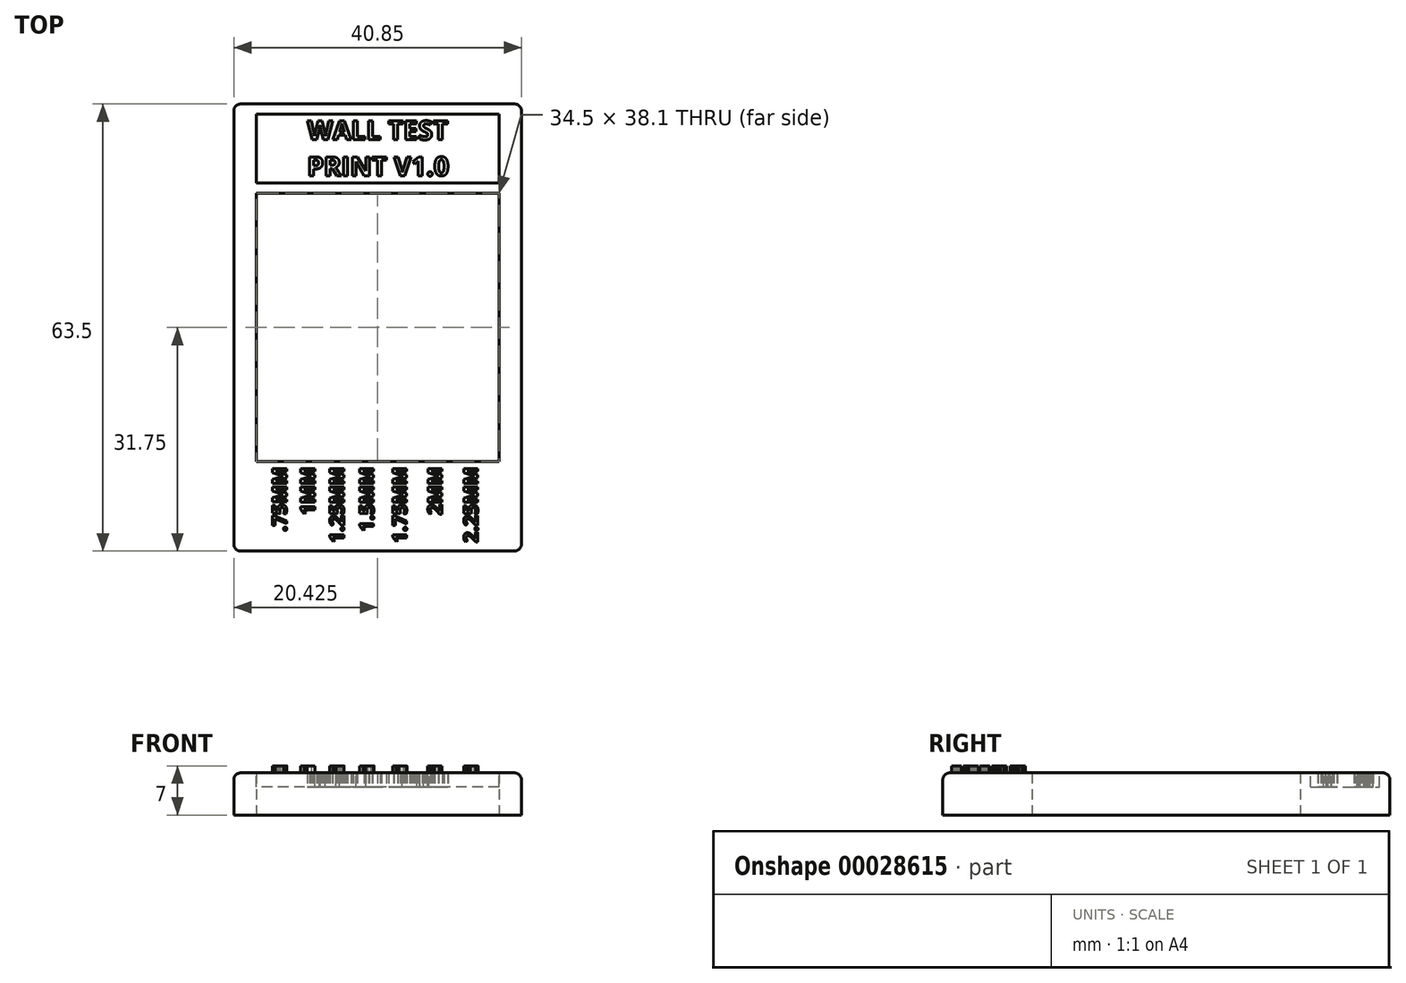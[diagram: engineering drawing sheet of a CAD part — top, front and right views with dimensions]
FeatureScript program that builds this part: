
annotation { "Feature Type Name" : "Feature", "Feature Type Description" : "" }
export const myFeature = defineFeature(function(context is Context, id is Id, definition is map)
    precondition{}
    {
        {
            var Q0;
            Q0=qCreatedBy(makeId("Top.planeOp"),FACE);
            var sketch = newSketch(context, id + "F0", { "sketchPlane" : qUnion([Q0])});
            skLineSegment(sketch, "E0.bottom", {"start": v(0, 0) * mm, "end": v(40.85, 0) * mm});
            skLineSegment(sketch, "E0.top", {"start": v(0, 63.5) * mm, "end": v(40.85, 63.5) * mm});
            skLineSegment(sketch, "E0.left", {"start": v(0, 0) * mm, "end": v(0, 63.5) * mm});
            skLineSegment(sketch, "E0.right", {"start": v(40.85, 0) * mm, "end": v(40.85, 63.5) * mm});
            skLineSegment(sketch, "E1.bottom", {"start": v(3.17, 12.7) * mm, "end": v(37.68, 12.7) * mm});
            skLineSegment(sketch, "E1.top", {"start": v(3.17, 50.8) * mm, "end": v(37.68, 50.8) * mm});
            skLineSegment(sketch, "E1.left", {"start": v(3.17, 12.7) * mm, "end": v(3.17, 50.8) * mm});
            skLineSegment(sketch, "E1.right", {"start": v(37.68, 12.7) * mm, "end": v(37.68, 50.8) * mm});
            skLineSegment(sketch, "E2.bottom", {"start": v(6.17, 50.8) * mm, "end": v(6.92, 50.8) * mm});
            skLineSegment(sketch, "E2.top", {"start": v(6.17, 12.7) * mm, "end": v(6.93, 12.7) * mm});
            skLineSegment(sketch, "E2.left", {"start": v(6.17, 50.8) * mm, "end": v(6.17, 12.7) * mm});
            skLineSegment(sketch, "E2.right", {"start": v(6.92, 50.8) * mm, "end": v(6.92, 12.7) * mm});
            skLineSegment(sketch, "E3.bottom", {"start": v(9.92, 50.8) * mm, "end": v(10.93, 50.8) * mm});
            skLineSegment(sketch, "E3.top", {"start": v(9.93, 12.7) * mm, "end": v(10.93, 12.7) * mm});
            skLineSegment(sketch, "E3.left", {"start": v(9.92, 50.8) * mm, "end": v(9.93, 12.7) * mm});
            skLineSegment(sketch, "E3.right", {"start": v(10.93, 50.8) * mm, "end": v(10.93, 12.7) * mm});
            skLineSegment(sketch, "E4.bottom", {"start": v(13.93, 50.8) * mm, "end": v(15.18, 50.8) * mm});
            skLineSegment(sketch, "E4.top", {"start": v(13.93, 12.7) * mm, "end": v(15.18, 12.7) * mm});
            skLineSegment(sketch, "E4.left", {"start": v(13.93, 50.8) * mm, "end": v(13.93, 12.7) * mm});
            skLineSegment(sketch, "E4.right", {"start": v(15.18, 50.8) * mm, "end": v(15.18, 12.7) * mm});
            skLineSegment(sketch, "E5.top", {"start": v(31.75, 12.7) * mm, "end": v(34.25, 12.7) * mm});
            skLineSegment(sketch, "E6.bottom", {"start": v(18.18, 50.8) * mm, "end": v(19.68, 50.8) * mm});
            skLineSegment(sketch, "E6.top", {"start": v(18.18, 12.7) * mm, "end": v(19.68, 12.7) * mm});
            skLineSegment(sketch, "E6.left", {"start": v(18.18, 50.8) * mm, "end": v(18.18, 12.7) * mm});
            skLineSegment(sketch, "E6.right", {"start": v(19.68, 50.8) * mm, "end": v(19.68, 12.7) * mm});
            skLineSegment(sketch, "E7.bottom", {"start": v(22.68, 50.8) * mm, "end": v(24.43, 50.8) * mm});
            skLineSegment(sketch, "E7.top", {"start": v(22.68, 12.7) * mm, "end": v(24.43, 12.7) * mm});
            skLineSegment(sketch, "E7.left", {"start": v(22.68, 50.8) * mm, "end": v(22.68, 12.7) * mm});
            skLineSegment(sketch, "E7.right", {"start": v(24.43, 50.8) * mm, "end": v(24.43, 12.7) * mm});
            skLineSegment(sketch, "E8.bottom", {"start": v(27.43, 50.8) * mm, "end": v(29.43, 50.8) * mm});
            skLineSegment(sketch, "E8.top", {"start": v(27.43, 12.7) * mm, "end": v(29.43, 12.7) * mm});
            skLineSegment(sketch, "E8.left", {"start": v(27.43, 50.8) * mm, "end": v(27.43, 12.7) * mm});
            skLineSegment(sketch, "E8.right", {"start": v(29.43, 50.8) * mm, "end": v(29.43, 12.7) * mm});
            skLineSegment(sketch, "E9.bottom", {"start": v(32.43, 50.8) * mm, "end": v(34.68, 50.8) * mm});
            skLineSegment(sketch, "E9.top", {"start": v(32.43, 12.7) * mm, "end": v(34.68, 12.7) * mm});
            skLineSegment(sketch, "E9.left", {"start": v(32.43, 50.8) * mm, "end": v(32.43, 12.7) * mm});
            skLineSegment(sketch, "E9.right", {"start": v(34.68, 50.8) * mm, "end": v(34.68, 12.7) * mm});
            skSolve(sketch);
        }
        {
            var Q0;
            Q0 = qSketchRegion(id + "F0", true);
            var Q1;
            Q1=makeQuery(id+"F0.imprint","IMPRINT",FACE,{"disambiguationData":[TD([[makeQuery(id+"F0.imprint","IMPRINT",EDGE,{"derivedFrom":sQuery(id+"F0.wireOp",EDGE,"E2.bottom")}),-1.0]])]});
            var Q2;
            Q2=makeQuery(id+"F0.imprint","IMPRINT",FACE,{"disambiguationData":[TD([[makeQuery(id+"F0.imprint","IMPRINT",EDGE,{"derivedFrom":sQuery(id+"F0.wireOp",EDGE,"E3.bottom")}),-1.0]])]});
            var Q3;
            Q3=makeQuery(id+"F0.imprint","IMPRINT",FACE,{"disambiguationData":[TD([[makeQuery(id+"F0.imprint","IMPRINT",EDGE,{"derivedFrom":sQuery(id+"F0.wireOp",EDGE,"E4.bottom")}),-1.0]])]});
            var Q4;
            Q4=makeQuery(id+"F0.imprint","IMPRINT",FACE,{"disambiguationData":[TD([[makeQuery(id+"F0.imprint","IMPRINT",EDGE,{"derivedFrom":sQuery(id+"F0.wireOp",EDGE,"E5.bottom")}),-1.0]])]});
            var Q5;
            Q5=makeQuery(id+"F0.imprint","IMPRINT",FACE,{"disambiguationData":[TD([[makeQuery(id+"F0.imprint","IMPRINT",EDGE,{"derivedFrom":sQuery(id+"F0.wireOp",EDGE,"E6.bottom")}),-1.0]])]});
            var Q6;
            Q6=makeQuery(id+"F0.imprint","IMPRINT",FACE,{"disambiguationData":[TD([[makeQuery(id+"F0.imprint","IMPRINT",EDGE,{"derivedFrom":sQuery(id+"F0.wireOp",EDGE,"E7.bottom")}),-1.0]])]});
            var Q7;
            Q7=makeQuery(id+"F0.imprint","IMPRINT",FACE,{"disambiguationData":[TD([[makeQuery(id+"F0.imprint","IMPRINT",EDGE,{"derivedFrom":sQuery(id+"F0.wireOp",EDGE,"E8.bottom")}),-1.0]])]});
            var Q8;
            Q8=makeQuery(id+"F0.imprint","IMPRINT",FACE,{"disambiguationData":[TD([[makeQuery(id+"F0.imprint","IMPRINT",EDGE,{"derivedFrom":sQuery(id+"F0.wireOp",EDGE,"E9.bottom")}),-1.0]])]});
            extrude(context, id + "F1", {"entities" : qUnion([Q0, Q1, Q2, Q3, Q4, Q5, Q6, Q7, Q8]), "depth" : 6 * mm});
        }
        {
            var Q0;
            Q0=makeQuery(id+"F1.opExtrude","CAP_FACE",FACE,{"disambiguationData":[OSD([sQuery(id+"F0.wireOp",EDGE,"E0.bottom"),sQuery(id+"F0.wireOp",EDGE,"E0.top"),sQuery(id+"F0.wireOp",EDGE,"E0.left"),sQuery(id+"F0.wireOp",EDGE,"E0.right"),sQuery(id+"F0.wireOp",EDGE,"E1.bottom"),sQuery(id+"F0.wireOp",EDGE,"E1.top"),sQuery(id+"F0.wireOp",EDGE,"E1.left"),sQuery(id+"F0.wireOp",EDGE,"E1.right"),sQuery(id+"F0.wireOp",EDGE,"E2.left"),sQuery(id+"F0.wireOp",EDGE,"E2.right"),sQuery(id+"F0.wireOp",EDGE,"E3.left"),sQuery(id+"F0.wireOp",EDGE,"E3.right"),sQuery(id+"F0.wireOp",EDGE,"E4.left"),sQuery(id+"F0.wireOp",EDGE,"E4.right"),sQuery(id+"F0.wireOp",EDGE,"E5.left"),sQuery(id+"F0.wireOp",EDGE,"E5.right"),sQuery(id+"F0.wireOp",EDGE,"E6.left"),sQuery(id+"F0.wireOp",EDGE,"E6.right")])],"isStart":false});
            var sketch = newSketch(context, id + "F2", { "sketchPlane" : qUnion([Q0])});
            skText(sketch, "E10", { "text": ".75MM", "fontName": "OpenSans-Bold.ttf"});
            const initialGuessF2  = {"E10": [0.00749, 0.00276, 0, 1, 0.002]};
            skSetInitialGuess(sketch, initialGuessF2);
            skSolve(sketch);
        }
        {
            var Q0;
            Q0 = qSketchRegion(id + "F2", true);
            var Q1;
            Q1 = qConstructionFilter(qBodyType(qCreatedBy(id + "F2" ,EDGE), BodyType.WIRE), ConstructionObject.NO);
            extrude(context, id + "F3", {"entities" : qUnion([Q0]), "operationType" : NewBodyOperationType.ADD, "surfaceEntities" : qUnion([Q1]), "depth" : 1 * mm});
        }
        {
            var Q0;
            Q0=makeQuery(id+"F1.opExtrude","CAP_FACE",FACE,{"disambiguationData":[OSD([sQuery(id+"F0.wireOp",EDGE,"E0.bottom"),sQuery(id+"F0.wireOp",EDGE,"E0.top"),sQuery(id+"F0.wireOp",EDGE,"E0.left"),sQuery(id+"F0.wireOp",EDGE,"E0.right"),sQuery(id+"F0.wireOp",EDGE,"E1.bottom"),sQuery(id+"F0.wireOp",EDGE,"E1.top"),sQuery(id+"F0.wireOp",EDGE,"E1.left"),sQuery(id+"F0.wireOp",EDGE,"E1.right"),sQuery(id+"F0.wireOp",EDGE,"E2.left"),sQuery(id+"F0.wireOp",EDGE,"E2.right"),sQuery(id+"F0.wireOp",EDGE,"E3.left"),sQuery(id+"F0.wireOp",EDGE,"E3.right"),sQuery(id+"F0.wireOp",EDGE,"E4.left"),sQuery(id+"F0.wireOp",EDGE,"E4.right"),sQuery(id+"F0.wireOp",EDGE,"E5.top"),sQuery(id+"F0.wireOp",EDGE,"E6.left"),sQuery(id+"F0.wireOp",EDGE,"E6.right"),sQuery(id+"F0.wireOp",EDGE,"E7.left"),sQuery(id+"F0.wireOp",EDGE,"E7.right"),sQuery(id+"F0.wireOp",EDGE,"E8.left"),sQuery(id+"F0.wireOp",EDGE,"E8.right"),sQuery(id+"F0.wireOp",EDGE,"E9.left"),sQuery(id+"F0.wireOp",EDGE,"E9.right")])],"isStart":false});
            var sketch = newSketch(context, id + "F4", { "sketchPlane" : qUnion([Q0])});
            skLineSegment(sketch, "E11", {"start": v(3.17, 50.8) * mm, "end": v(3.17, 63.5) * mm, "construction": true});
            skLineSegment(sketch, "E12", {"start": v(37.68, 50.8) * mm, "end": v(37.68, 63.5) * mm, "construction": true});
            skLineSegment(sketch, "E13", {"start": v(3.17, 57.15) * mm, "end": v(37.68, 57.15) * mm, "construction": true});
            skLineSegment(sketch, "E14", {"start": v(20.42, 57.15) * mm, "end": v(20.42, 63.5) * mm, "construction": true});
            skLineSegment(sketch, "E15.rect.bottom", {"start": v(37.67, 52.25) * mm, "end": v(3.18, 52.25) * mm});
            skLineSegment(sketch, "E15.rect.top", {"start": v(37.68, 62.05) * mm, "end": v(3.18, 62.05) * mm});
            skLineSegment(sketch, "E15.rect.left", {"start": v(37.68, 52.25) * mm, "end": v(37.68, 62.05) * mm});
            skLineSegment(sketch, "E15.rect.right", {"start": v(3.18, 52.25) * mm, "end": v(3.18, 62.05) * mm});
            skPoint(sketch, "E15.rect.middle", {"position": v(20.42, 57.15) * mm});
            skSolve(sketch);
        }
        {
            var Q0;
            Q0 = qSketchRegion(id + "F4", true);
            extrude(context, id + "F5", {"entities" : qUnion([Q0]), "operationType" : NewBodyOperationType.REMOVE, "oppositeDirection" : true, "depth" : 2 * mm});
        }
        {
            var Q0;
            Q0=makeQuery(id+"F5.boolean.opBoolean","COPY",FACE,{"derivedFrom":makeQuery(id+"F5.opExtrude","CAP_FACE",FACE,{"disambiguationData":[OSD([sQuery(id+"F4.wireOp",EDGE,"E15.rect.bottom"),sQuery(id+"F4.wireOp",EDGE,"E15.rect.top"),sQuery(id+"F4.wireOp",EDGE,"E15.rect.left"),sQuery(id+"F4.wireOp",EDGE,"E15.rect.right")])],"isStart":false})});
            var sketch = newSketch(context, id + "F6", { "sketchPlane" : qUnion([Q0])});
            skText(sketch, "E16", { "text": "WALL TEST\nPRINT V1.0", "fontName": "OpenSans-Bold.ttf"});
            skLineSegment(sketch, "E17", {"start": v(20.43, 62.05) * mm, "end": v(20.43, 52.25) * mm, "construction": true});
            const initialGuessF6  = {"E16": [0.01043, 0.05842, 1, 0, 0.00271]};
            skSetInitialGuess(sketch, initialGuessF6);
            skSolve(sketch);
        }
        {
            var Q0;
            Q0 = qSketchRegion(id + "F6", true);
            extrude(context, id + "F7", {"entities" : qUnion([Q0]), "operationType" : NewBodyOperationType.ADD, "depth" : 2 * mm});
        }
        {
            var Q0;
            Q0=makeQuery(id+"F1.opExtrude","CAP_FACE",FACE,{"disambiguationData":[OSD([sQuery(id+"F0.wireOp",EDGE,"E0.bottom"),sQuery(id+"F0.wireOp",EDGE,"E0.top"),sQuery(id+"F0.wireOp",EDGE,"E0.left"),sQuery(id+"F0.wireOp",EDGE,"E0.right"),sQuery(id+"F0.wireOp",EDGE,"E1.bottom"),sQuery(id+"F0.wireOp",EDGE,"E1.top"),sQuery(id+"F0.wireOp",EDGE,"E1.left"),sQuery(id+"F0.wireOp",EDGE,"E1.right"),sQuery(id+"F0.wireOp",EDGE,"E2.left"),sQuery(id+"F0.wireOp",EDGE,"E2.right"),sQuery(id+"F0.wireOp",EDGE,"E3.left"),sQuery(id+"F0.wireOp",EDGE,"E3.right"),sQuery(id+"F0.wireOp",EDGE,"E4.left"),sQuery(id+"F0.wireOp",EDGE,"E4.right"),sQuery(id+"F0.wireOp",EDGE,"E5.top"),sQuery(id+"F0.wireOp",EDGE,"E6.left"),sQuery(id+"F0.wireOp",EDGE,"E6.right"),sQuery(id+"F0.wireOp",EDGE,"E7.left"),sQuery(id+"F0.wireOp",EDGE,"E7.right"),sQuery(id+"F0.wireOp",EDGE,"E8.left"),sQuery(id+"F0.wireOp",EDGE,"E8.right"),sQuery(id+"F0.wireOp",EDGE,"E9.left"),sQuery(id+"F0.wireOp",EDGE,"E9.right")])],"isStart":false});
            var sketch = newSketch(context, id + "F8", { "sketchPlane" : qUnion([Q0])});
            skText(sketch, "E18", { "text": "1MM", "fontName": "OpenSans-Bold.ttf"});
            skText(sketch, "E19", { "text": "1.25MM", "fontName": "OpenSans-Bold.ttf"});
            skText(sketch, "E20", { "text": "1.5MM", "fontName": "OpenSans-Bold.ttf"});
            skText(sketch, "E21", { "text": "1.75MM", "fontName": "OpenSans-Bold.ttf"});
            skText(sketch, "E22", { "text": "2MM", "fontName": "OpenSans-Bold.ttf"});
            skText(sketch, "E23", { "text": "2.25MM", "fontName": "OpenSans-Bold.ttf"});
            skLineSegment(sketch, "E24", {"start": v(20.43, 0) * mm, "end": v(20.43, 12.7) * mm, "construction": true});
            skLineSegment(sketch, "E25", {"start": v(40.31, 11.7) * mm, "end": v(-5.56, 11.7) * mm, "construction": true});
            const initialGuessF8  = {"E18": [0.0115, 0.00513, 0, 1, 0.002], "E19": [0.01563, 0.00116, 0, 1, 0.002], "E20": [0.01987, 0.00275, 0, 1, 0.002], "E21": [0.02455, 0.00116, 0, 1, 0.002], "E22": [0.02956, 0.00513, 0, 1, 0.002], "E23": [0.03466, 0.00116, 0, 1, 0.002]};
            skSetInitialGuess(sketch, initialGuessF8);
            skSolve(sketch);
        }
        {
            var Q0;
            Q0=makeQuery(id+"F1.opExtrude","CAP_EDGE",EDGE,{"disambiguationData":[OSD([sQuery(id+"F0.wireOp",EDGE,"E0.right")])],"isStart":false});
            var Q1;
            Q1=makeQuery(id+"F1.opExtrude","CAP_EDGE",EDGE,{"disambiguationData":[OSD([sQuery(id+"F0.wireOp",EDGE,"E0.left")])],"isStart":false});
            var Q2;
            Q2=makeQuery(id+"F1.opExtrude","CAP_EDGE",EDGE,{"disambiguationData":[OSD([sQuery(id+"F0.wireOp",EDGE,"E0.bottom")])],"isStart":false});
            var Q3;
            Q3=makeQuery(id+"F1.opExtrude","CAP_EDGE",EDGE,{"disambiguationData":[OSD([sQuery(id+"F0.wireOp",EDGE,"E0.top")])],"isStart":false});
            var Q4;
            Q4=makeQuery(id+"F1.opExtrude","SWEPT_EDGE",EDGE,{"disambiguationData":[OSD([sQuery(id+"F0.wireOp",EDGE,"E0.bottom"),sQuery(id+"F0.wireOp",EDGE,"E0.right")])]});
            var Q5;
            Q5=makeQuery(id+"F1.opExtrude","SWEPT_EDGE",EDGE,{"disambiguationData":[OSD([sQuery(id+"F0.wireOp",EDGE,"E0.bottom"),sQuery(id+"F0.wireOp",EDGE,"E0.left")])]});
            var Q6;
            Q6=makeQuery(id+"F1.opExtrude","SWEPT_EDGE",EDGE,{"disambiguationData":[OSD([sQuery(id+"F0.wireOp",EDGE,"E0.top"),sQuery(id+"F0.wireOp",EDGE,"E0.left")])]});
            var Q7;
            Q7=makeQuery(id+"F1.opExtrude","SWEPT_EDGE",EDGE,{"disambiguationData":[OSD([sQuery(id+"F0.wireOp",EDGE,"E0.top"),sQuery(id+"F0.wireOp",EDGE,"E0.right")])]});
            fillet(context, id + "F9", {"entities" : qUnion([Q0, Q1, Q2, Q3, Q4, Q5, Q6, Q7]), "radius" : 1 * mm, "tangentPropagation" : true, "allowEdgeOverflow" : false});
        }
        {
            var Q0;
            Q0 = qSketchRegion(id + "F8", true);
            extrude(context, id + "F10", {"entities" : qUnion([Q0]), "operationType" : NewBodyOperationType.ADD, "depth" : 1 * mm});
        }
    });
